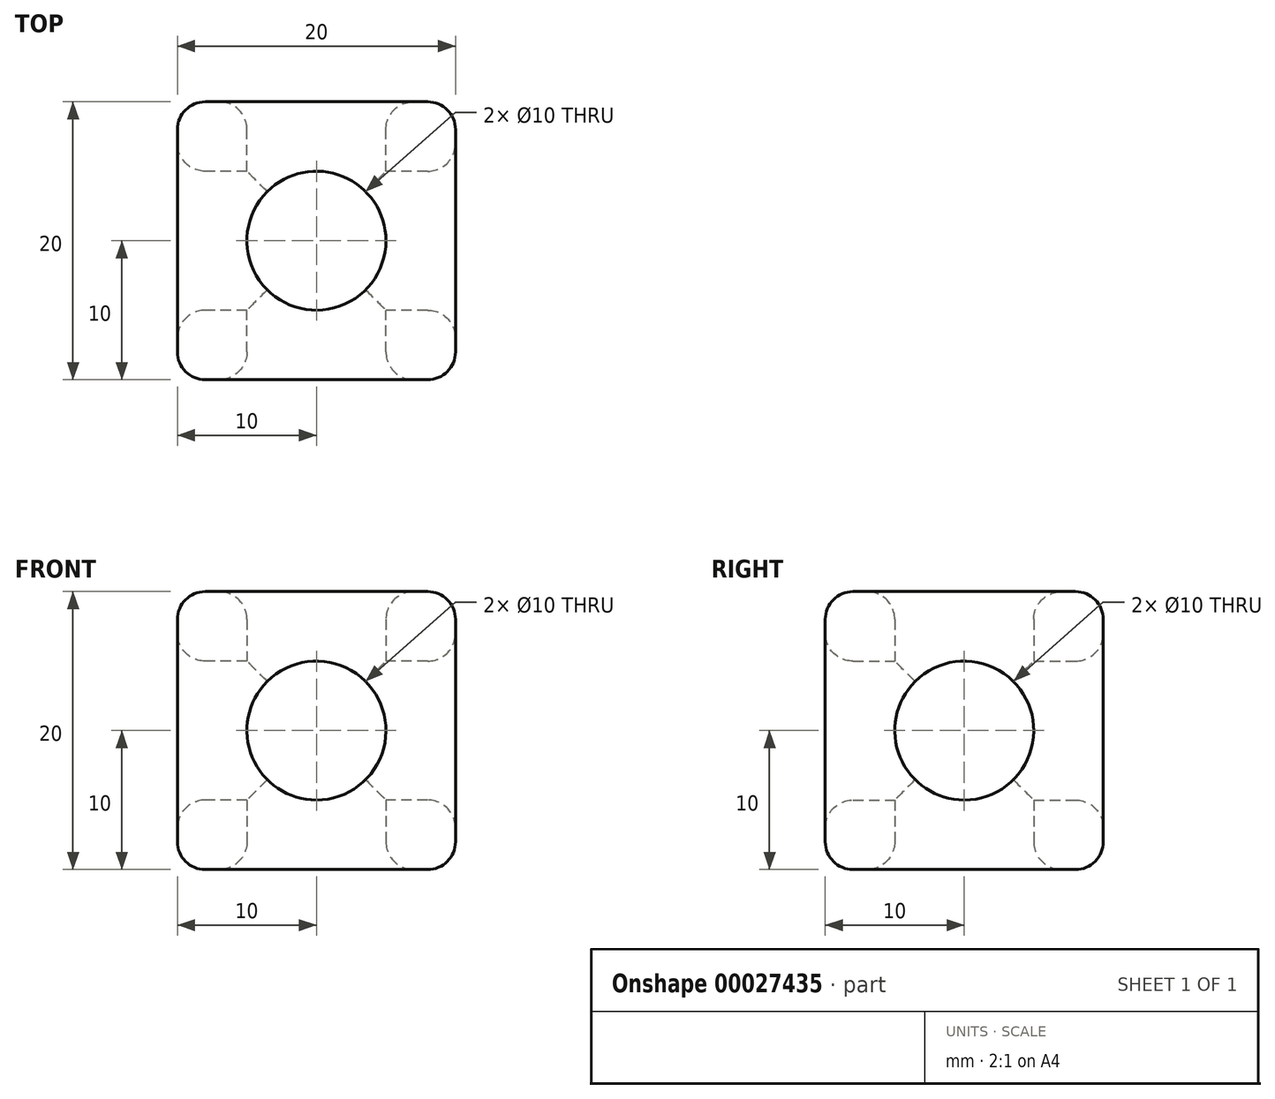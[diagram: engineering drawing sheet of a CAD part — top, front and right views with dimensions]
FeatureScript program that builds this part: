
annotation { "Feature Type Name" : "Feature", "Feature Type Description" : "" }
export const myFeature = defineFeature(function(context is Context, id is Id, definition is map)
    precondition{}
    {
        {
            var Q0;
            Q0=qCreatedBy(makeId("Top.planeOp"),FACE);
            var sketch = newSketch(context, id + "F0", { "sketchPlane" : qUnion([Q0])});
            skLineSegment(sketch, "E0.rect.bottom", {"start": v(10, 10) * mm, "end": v(-10, 10) * mm});
            skLineSegment(sketch, "E0.rect.top", {"start": v(10, -10) * mm, "end": v(-10, -10) * mm});
            skLineSegment(sketch, "E0.rect.left", {"start": v(10, 10) * mm, "end": v(10, -10) * mm});
            skLineSegment(sketch, "E0.rect.right", {"start": v(-10, 10) * mm, "end": v(-10, -10) * mm});
            skPoint(sketch, "E0.rect.middle", {"position": v(0, 0) * mm});
            skCircle(sketch, "E1", {"center": v(0, 0) * mm, "radius": 5 * mm});
            skSolve(sketch);
        }
        {
            var Q0;
            Q0 = qSketchRegion(id + "F0", true);
            extrude(context, id + "F1", {"entities" : qUnion([Q0]), "depth" : 20 * mm});
        }
        {
            var Q0;
            Q0=makeQuery(id+"F1.opExtrude","SWEPT_FACE",FACE,{"disambiguationData":[OSD([sQuery(id+"F0.wireOp",EDGE,"E0.rect.right")])]});
            var sketch = newSketch(context, id + "F2", { "sketchPlane" : qUnion([Q0])});
            skCircle(sketch, "E2", {"center": v(0, 10) * mm, "radius": 5 * mm});
            skPoint(sketch, "E2.centerSnap0", {"position": v(-10, 10) * mm});
            skPoint(sketch, "E2.centerSnap1", {"position": v(0, 20) * mm});
            skSolve(sketch);
        }
        {
            var Q0;
            Q0 = qSketchRegion(id + "F2", true);
            extrude(context, id + "F3", {"entities" : qUnion([Q0]), "operationType" : NewBodyOperationType.REMOVE, "oppositeDirection" : true, "depth" : 25 * mm});
        }
        {
            var Q0;
            Q0=makeQuery(id+"F1.opExtrude","SWEPT_FACE",FACE,{"disambiguationData":[OSD([sQuery(id+"F0.wireOp",EDGE,"E0.rect.bottom")])]});
            var sketch = newSketch(context, id + "F4", { "sketchPlane" : qUnion([Q0])});
            skCircle(sketch, "E3", {"center": v(0, 10) * mm, "radius": 5 * mm});
            skPoint(sketch, "E3.centerSnap0", {"position": v(10, 10) * mm});
            skSolve(sketch);
        }
        {
            var Q0;
            Q0=makeQuery(id+"F4.imprint","IMPRINT",FACE,{"disambiguationData":[TD([[makeQuery(id+"F4.imprint","IMPRINT",EDGE,{"derivedFrom":sQuery(id+"F4.wireOp",EDGE,"E3")}),1.0]])]});
            extrude(context, id + "F5", {"entities" : qUnion([Q0]), "operationType" : NewBodyOperationType.REMOVE, "oppositeDirection" : true, "depth" : 25 * mm});
        }
        {
            var Q0;
            Q0=makeQuery(id+"F1.opExtrude","SWEPT_FACE",FACE,{"disambiguationData":[OSD([sQuery(id+"F0.wireOp",EDGE,"E0.rect.right")])]});
            var Q1;
            Q1=makeQuery(id+"F1.opExtrude","SWEPT_FACE",FACE,{"disambiguationData":[OSD([sQuery(id+"F0.wireOp",EDGE,"E0.rect.top")])]});
            var Q2;
            Q2=makeQuery(id+"F1.opExtrude","SWEPT_FACE",FACE,{"disambiguationData":[OSD([sQuery(id+"F0.wireOp",EDGE,"E0.rect.left")])]});
            var Q3;
            Q3=makeQuery(id+"F1.opExtrude","CAP_FACE",FACE,{"disambiguationData":[OSD([sQuery(id+"F0.wireOp",EDGE,"E0.rect.bottom"),sQuery(id+"F0.wireOp",EDGE,"E0.rect.top"),sQuery(id+"F0.wireOp",EDGE,"E0.rect.left"),sQuery(id+"F0.wireOp",EDGE,"E0.rect.right"),sQuery(id+"F0.wireOp",EDGE,"E1")])],"isStart":true});
            var Q4;
            Q4=makeQuery(id+"F1.opExtrude","SWEPT_FACE",FACE,{"disambiguationData":[OSD([sQuery(id+"F0.wireOp",EDGE,"E0.rect.bottom")])]});
            var Q5;
            Q5=makeQuery(id+"F1.opExtrude","CAP_FACE",FACE,{"disambiguationData":[OSD([sQuery(id+"F0.wireOp",EDGE,"E0.rect.bottom"),sQuery(id+"F0.wireOp",EDGE,"E0.rect.top"),sQuery(id+"F0.wireOp",EDGE,"E0.rect.left"),sQuery(id+"F0.wireOp",EDGE,"E0.rect.right"),sQuery(id+"F0.wireOp",EDGE,"E1")])],"isStart":false});
            fillet(context, id + "F6", {"entities" : qUnion([Q0, Q1, Q2, Q3, Q4, Q5]), "radius" : 2 * mm, "tangentPropagation" : true, "allowEdgeOverflow" : false});
        }
    });
